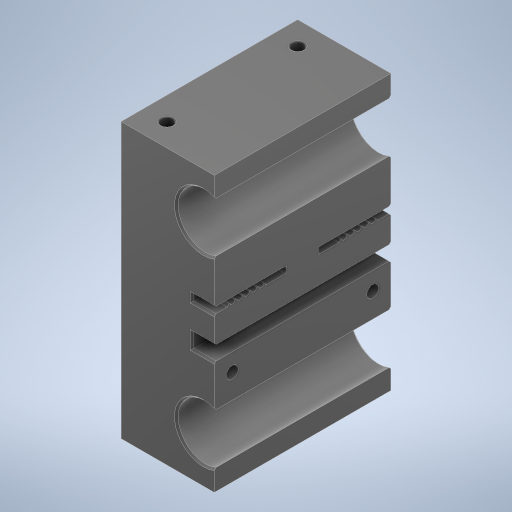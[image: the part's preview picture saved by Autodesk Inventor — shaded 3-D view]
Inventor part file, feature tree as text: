
AUTODESK INVENTOR PART (.ipt)
format: ipt  version: 2023 (Build 270158000, 158)  size: 829,440 bytes
history: native  units: in
note: dims shown in document units (in); Inventor stores cm internally (conversion verified against a paired STEP export)
features: sketch x7, extrude x5, chamfer x4, fillet x4, plane x2, hole x2, projected_geometry x1
ambient origin geometry x8: Origin, YZ Plane, XZ Plane, XY Plane, X Axis, Y Axis, Z Axis, Center Point
bodies: Solid1 (feature_tree)
feature tree (25):
  extrude  "Extrusion1"  Depth=0.5956in
  chamfer  "Chamfer1"  Distance=1.9291in
  plane  "Work Plane2"
  extrude  "Extrusion3"  Depth=0.7087in TaperAngle=45.0deg
  extrude  "Extrusion4"  Depth=0.7087in TaperAngle=0.0deg
  fillet  "Fillet1"  Radius=1.0in
  fillet  "Fillet2"  Radius=0.7874in
  chamfer  "Chamfer2"  Distance=0.06in
  extrude  "Extrusion5"  Depth=0.7087in
  chamfer  "Chamfer3"  Distance=0.1181in
  hole  "Hole1"  [1 undecoded]
  fillet  "Fillet3"  Radius=0.0787in
  extrude  "Extrusion6"  Depth=0.7087in
  fillet  "Fillet4"  Radius=0.0787in
  chamfer  "Chamfer4"  Distance=0.0787in
  hole  "Hole2"  [1 undecoded]
  sketch  "Sketch1"  dims[d0=3.0in d1=0.5956in]
  plane  "Work Plane1"
  sketch  "Sketch4"  dims[d2=0.5956in]
  sketch  "Sketch5"  dims[d3=1.8in]
  sketch  "Sketch7"  dims[d4=0.5in]
  sketch  "Sketch8"  dims[d5=2.0in]
  sketch  "Sketch9"  dims[d7=0.5in]
  sketch  "Sketch10"  dims[d8=0.0in d9=1.9291in d10=0.0in d11=0.02in d12=0.125in d13=45.0deg d25=0.0in d26=0.1181in d27=1.0in d28=0.0in d29=0.7874in d30=0.06in d32=0.0299in d33=0.1181in d34=0.0787in d35=0.0787in d36=0.0787in d37=0.0787in d38=0.0787in d39=0.0787in d40=0.026in d41=0.026in d43=0.026in d44=0.026in d45=0.026in d46=0.026in d47=0.026in d48=0.026in d49=0.026in d50=0.026in d51=0.026in d52=0.026in d53=0.0039in d54=0.0039in d55=60.0deg d56=0.0008in d57=60.0deg d58=0.0008in d59=0.2441in d60=0.0in d61=0.0118in d62=0.0079in d63=0.4758in d66=1.9291in d67=0.0079in d68=0.0197in d69=0.0492in d70=45.0deg d71=0.3707in d72=0.1575in d73=0.0787in d74=0.2441in d75=0.0in d76=0.0197in d77=0.0492in d78=45.0deg d79=0.1588in d80=0.25in d81=0.25in d82=0.25in d83=0.25in d84=0.1339in d85=0.198in d86=0.2559in d87=0.1181in d88=90.0deg d89=0.3937in d90=0.8108in d91=0.0079in d92=0.315in d93=0.0984in d94=0.2756in d95=0.5256in d96=0.0in d97=0.0079in d98=0.0197in d99=0.0492in d100=45.0deg d101=0.1969in d102=0.1969in d103=0.1969in d104=0.1969in d105=0.1339in d106=0.2953in d107=0.2559in d108=0.7087in d109=90.0deg d110=0.346in d111=0.8108in]
  projected_geometry  "Projected Loop2"
note: 2 required parameter values undecoded (feature->parameter linkage not recoverable at this tier; creation-order binding heuristic only, values carry confidence <= 0.55)
